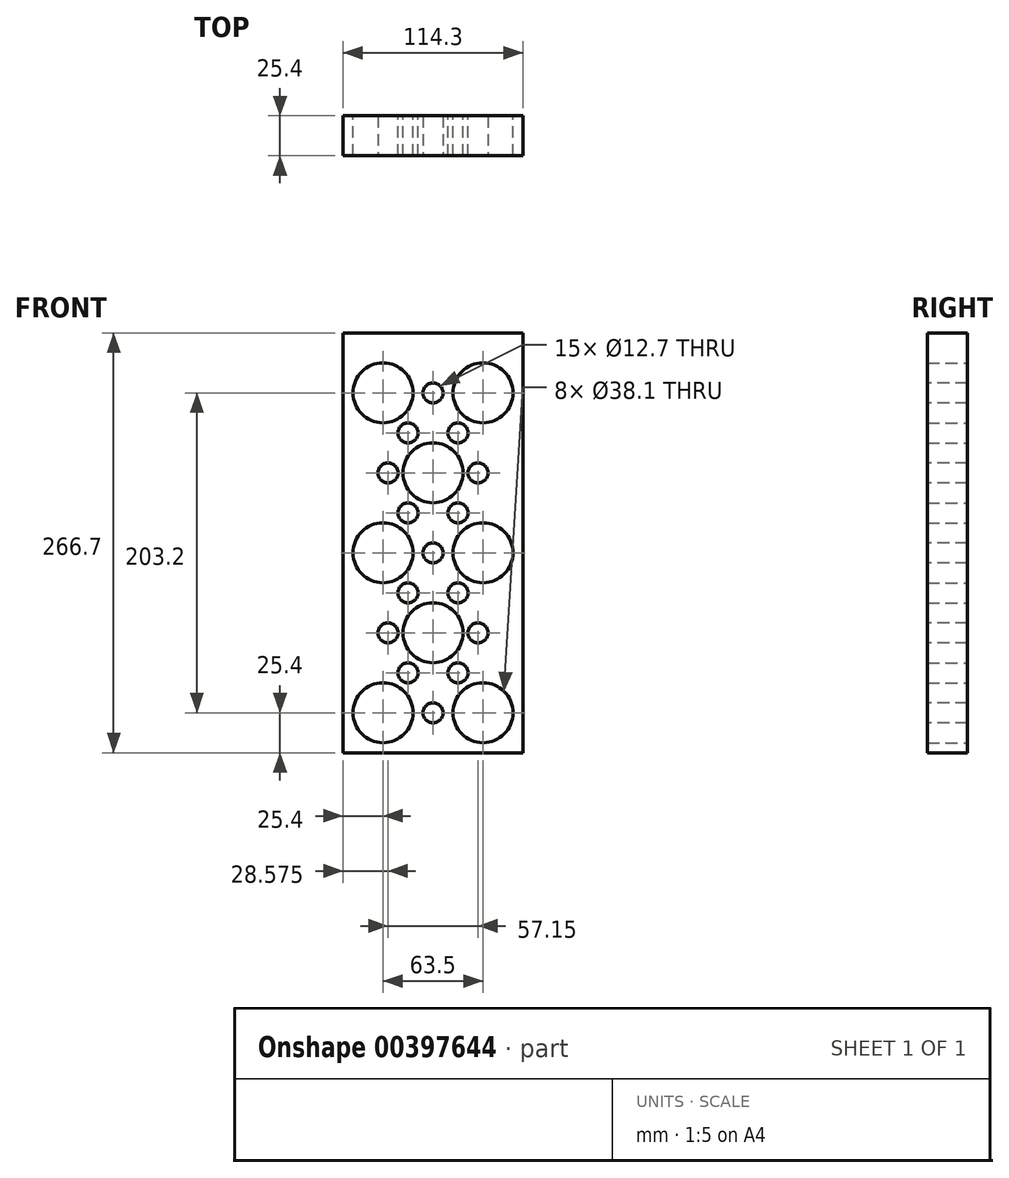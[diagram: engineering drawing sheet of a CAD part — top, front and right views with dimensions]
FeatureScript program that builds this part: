
annotation { "Feature Type Name" : "Feature", "Feature Type Description" : "" }
export const myFeature = defineFeature(function(context is Context, id is Id, definition is map)
    precondition{}
    {
        {
            var Q0;
            Q0=qCreatedBy(makeId("Front.planeOp"),FACE);
            var sketch = newSketch(context, id + "F0", { "sketchPlane" : qUnion([Q0])});
            skLineSegment(sketch, "E0.bottom", {"start": v(0, 0) * mm, "end": v(-114.3, 0) * mm});
            skLineSegment(sketch, "E0.top", {"start": v(0, 266.7) * mm, "end": v(-114.3, 266.7) * mm});
            skLineSegment(sketch, "E0.left", {"start": v(0, 0) * mm, "end": v(0, 266.7) * mm});
            skLineSegment(sketch, "E0.right", {"start": v(-114.3, 0) * mm, "end": v(-114.3, 266.7) * mm});
            skSolve(sketch);
        }
        {
            var Q0;
            Q0=makeQuery(id+"F0.imprint","IMPRINT",FACE,{"disambiguationData":[TD([[makeQuery(id+"F0.imprint","IMPRINT",EDGE,{"derivedFrom":sQuery(id+"F0.wireOp",EDGE,"E0.bottom")}),-1.0]])]});
            var sketch = newSketch(context, id + "F1", { "sketchPlane" : qUnion([Q0])});
            skLineSegment(sketch, "E1", {"start": v(0, 0) * mm, "end": v(-25.4, 0) * mm});
            skLineSegment(sketch, "E2", {"start": v(0, 0) * mm, "end": v(-57.15, 0) * mm});
            skLineSegment(sketch, "E3", {"start": v(0, 0) * mm, "end": v(-88.9, 0) * mm});
            skLineSegment(sketch, "E4", {"start": v(0, 0) * mm, "end": v(-114.3, 0) * mm});
            skLineSegment(sketch, "E5", {"start": v(-88.9, 0) * mm, "end": v(-88.9, 25.4) * mm});
            skLineSegment(sketch, "E6", {"start": v(-25.4, 0) * mm, "end": v(-25.4, 25.4) * mm});
            skCircle(sketch, "E7", {"center": v(-88.9, 25.4) * mm, "radius": 19.05 * mm});
            skCircle(sketch, "E8", {"center": v(-25.4, 25.4) * mm, "radius": 19.05 * mm});
            skLineSegment(sketch, "E9", {"start": v(-57.15, 0) * mm, "end": v(-57.15, 31.75) * mm});
            skLineSegment(sketch, "E10", {"start": v(-57.15, 0) * mm, "end": v(-57.15, 63.5) * mm});
            skLineSegment(sketch, "E11", {"start": v(-88.9, 0) * mm, "end": v(-88.9, 50.8) * mm});
            skLineSegment(sketch, "E12", {"start": v(-25.4, 0) * mm, "end": v(-25.4, 50.8) * mm});
            skLineSegment(sketch, "E13", {"start": v(-88.9, 50.8) * mm, "end": v(-73.03, 50.8) * mm});
            skLineSegment(sketch, "E14", {"start": v(-25.4, 50.8) * mm, "end": v(-41.28, 50.8) * mm});
            skCircle(sketch, "E15", {"center": v(-73.03, 50.8) * mm, "radius": 6.35 * mm});
            skCircle(sketch, "E16", {"center": v(-41.28, 50.8) * mm, "radius": 6.35 * mm});
            skLineSegment(sketch, "E17", {"start": v(-57.15, 0) * mm, "end": v(-57.15, 76.2) * mm});
            skCircle(sketch, "E18", {"center": v(-57.15, 76.2) * mm, "radius": 19.05 * mm});
            skCircle(sketch, "E19.0.1.0", {"center": v(-73.02, 101.6) * mm, "radius": 6.35 * mm});
            skCircle(sketch, "E19.0.1.1", {"center": v(-41.28, 101.6) * mm, "radius": 6.35 * mm});
            skCircle(sketch, "E19.0.2.0", {"center": v(-73.02, 152.4) * mm, "radius": 6.35 * mm});
            skCircle(sketch, "E19.0.2.1", {"center": v(-41.28, 152.4) * mm, "radius": 6.35 * mm});
            skLineSegment(sketch, "E19.direction1", {"start": v(-73.03, 50.8) * mm, "end": v(-47.63, 50.8) * mm, "construction": true});
            skLineSegment(sketch, "E19.direction2", {"start": v(-73.03, 50.8) * mm, "end": v(-73.03, 101.6) * mm, "construction": true});
            skCircle(sketch, "E20.0.1.0", {"center": v(-88.9, 127) * mm, "radius": 19.05 * mm});
            skCircle(sketch, "E20.0.1.1", {"center": v(-25.4, 127) * mm, "radius": 19.05 * mm});
            skLineSegment(sketch, "E20.direction1", {"start": v(-88.9, 25.4) * mm, "end": v(-63.5, 25.4) * mm, "construction": true});
            skLineSegment(sketch, "E20.direction2", {"start": v(-88.9, 25.4) * mm, "end": v(-88.9, 127) * mm, "construction": true});
            skCircle(sketch, "E21.0.0.3", {"center": v(-73.02, 203.2) * mm, "radius": 6.35 * mm});
            skCircle(sketch, "E21.2.0.3", {"center": v(-41.28, 203.2) * mm, "radius": 6.35 * mm});
            skCircle(sketch, "E22.0.1.0", {"center": v(-57.15, 177.8) * mm, "radius": 19.05 * mm});
            skLineSegment(sketch, "E22.direction1", {"start": v(-57.15, 76.2) * mm, "end": v(-31.75, 76.2) * mm, "construction": true});
            skLineSegment(sketch, "E22.direction2", {"start": v(-57.15, 76.2) * mm, "end": v(-57.15, 177.8) * mm, "construction": true});
            skCircle(sketch, "E23.0.0.2", {"center": v(-88.9, 228.6) * mm, "radius": 19.05 * mm});
            skCircle(sketch, "E23.2.0.2", {"center": v(-25.4, 228.6) * mm, "radius": 19.05 * mm});
            skSolve(sketch);
        }
        {
            var Q0;
            Q0 = qSketchRegion(id + "F0", true);
            extrude(context, id + "F2", {"entities" : qUnion([Q0]), "depth" : 25.4 * mm});
        }
        {
            var Q0;
            Q0 = qSketchRegion(id + "F1", true);
            extrude(context, id + "F3", {"entities" : qUnion([Q0]), "operationType" : NewBodyOperationType.REMOVE, "depth" : 25.4 * mm});
        }
        {
            var Q0;
            Q0=makeQuery(id+"F2.opExtrude","CAP_FACE",FACE,{"disambiguationData":[OSD([sQuery(id+"F0.wireOp",EDGE,"E0.bottom"),sQuery(id+"F0.wireOp",EDGE,"E0.top"),sQuery(id+"F0.wireOp",EDGE,"E0.left"),sQuery(id+"F0.wireOp",EDGE,"E0.right")])],"isStart":false});
            var sketch = newSketch(context, id + "F4", { "sketchPlane" : qUnion([Q0])});
            skSolve(sketch);
        }
        {
            var Q0;
            Q0=makeQuery(id+"F4.imprint","IMPRINT",FACE,{"disambiguationData":[TD([[makeQuery(id+"F4.imprint","IMPRINT",EDGE,{"derivedFrom":makeQuery(id+"F2.opExtrude","CAP_EDGE",EDGE,{"disambiguationData":[OSD([sQuery(id+"F0.wireOp",EDGE,"E0.bottom")])],"isStart":false})}),-1.0]])]});
            var sketch = newSketch(context, id + "F5", { "sketchPlane" : qUnion([Q0])});
            skLineSegment(sketch, "E24", {"start": v(0, 0) * mm, "end": v(-28.58, 0) * mm});
            skLineSegment(sketch, "E25", {"start": v(0, 0) * mm, "end": v(-57.15, 0) * mm});
            skLineSegment(sketch, "E26", {"start": v(0, 0) * mm, "end": v(-85.73, 0) * mm});
            skLineSegment(sketch, "E27", {"start": v(-57.15, 0) * mm, "end": v(-57.15, 25.4) * mm});
            skLineSegment(sketch, "E28", {"start": v(-85.73, 0) * mm, "end": v(-85.73, 76.2) * mm});
            skLineSegment(sketch, "E29", {"start": v(-28.58, 0) * mm, "end": v(-28.58, 76.2) * mm});
            skCircle(sketch, "E30", {"center": v(-57.15, 25.4) * mm, "radius": 6.35 * mm});
            skCircle(sketch, "E31", {"center": v(-85.73, 76.2) * mm, "radius": 6.35 * mm});
            skCircle(sketch, "E32", {"center": v(-28.58, 76.2) * mm, "radius": 6.35 * mm});
            skCircle(sketch, "E33.0.1.0", {"center": v(-85.73, 177.8) * mm, "radius": 6.35 * mm});
            skCircle(sketch, "E33.0.1.1", {"center": v(-28.58, 177.8) * mm, "radius": 6.35 * mm});
            skLineSegment(sketch, "E33.direction1", {"start": v(-85.73, 76.2) * mm, "end": v(-60.33, 76.2) * mm, "construction": true});
            skLineSegment(sketch, "E33.direction2", {"start": v(-85.73, 76.2) * mm, "end": v(-85.73, 177.8) * mm, "construction": true});
            skCircle(sketch, "E34.0.1.0", {"center": v(-57.15, 127) * mm, "radius": 6.35 * mm});
            skCircle(sketch, "E34.0.2.0", {"center": v(-57.15, 228.6) * mm, "radius": 6.35 * mm});
            skLineSegment(sketch, "E34.direction1", {"start": v(-57.15, 25.4) * mm, "end": v(-31.75, 25.4) * mm, "construction": true});
            skLineSegment(sketch, "E34.direction2", {"start": v(-57.15, 25.4) * mm, "end": v(-57.15, 127) * mm, "construction": true});
            skSolve(sketch);
        }
        {
            var Q0;
            Q0 = qSketchRegion(id + "F5", true);
            extrude(context, id + "F6", {"entities" : qUnion([Q0]), "operationType" : NewBodyOperationType.REMOVE, "oppositeDirection" : true, "depth" : 25.4 * mm});
        }
    });
